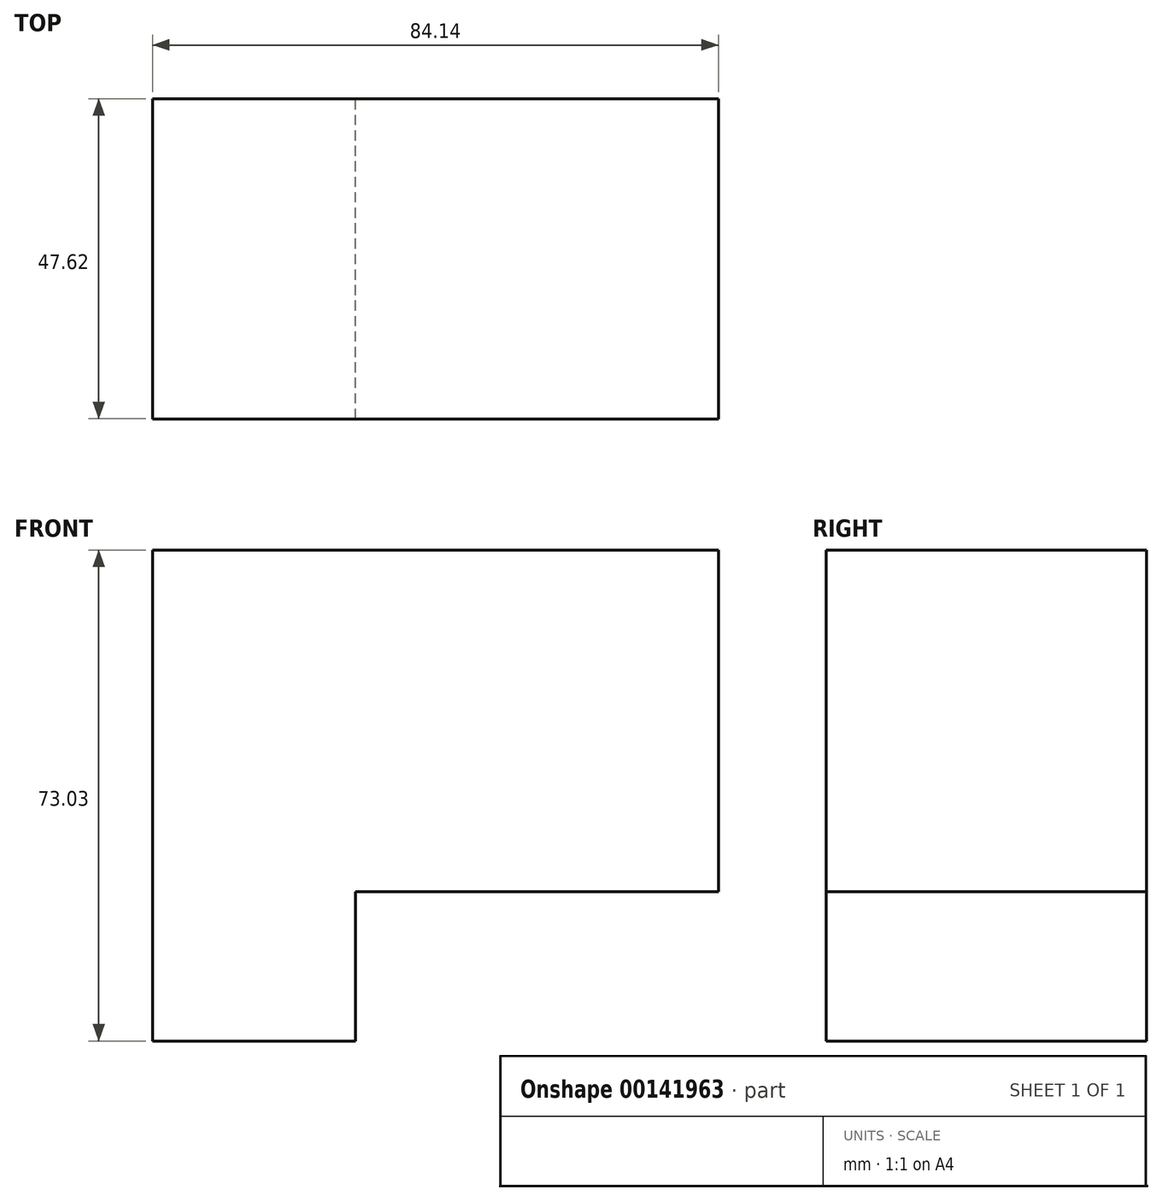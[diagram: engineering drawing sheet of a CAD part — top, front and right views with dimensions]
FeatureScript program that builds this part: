
annotation { "Feature Type Name" : "Feature", "Feature Type Description" : "" }
export const myFeature = defineFeature(function(context is Context, id is Id, definition is map)
    precondition{}
    {
        {
            var Q0;
            Q0=qCreatedBy(makeId("Front.planeOp"),FACE);
            var sketch = newSketch(context, id + "F0", { "sketchPlane" : qUnion([Q0])});
            skLineSegment(sketch, "E0.bottom", {"start": v(-30.16, 50.8) * mm, "end": v(0, 50.8) * mm});
            skLineSegment(sketch, "E0.top", {"start": v(-30.16, -22.23) * mm, "end": v(0, -22.23) * mm});
            skLineSegment(sketch, "E0.left", {"start": v(-30.16, 50.8) * mm, "end": v(-30.16, -22.23) * mm});
            skLineSegment(sketch, "E0.right", {"start": v(0, 50.8) * mm, "end": v(0, -22.23) * mm});
            skLineSegment(sketch, "E1.bottom", {"start": v(0, 50.8) * mm, "end": v(53.97, 50.8) * mm});
            skLineSegment(sketch, "E1.top", {"start": v(0, 0) * mm, "end": v(53.97, 0) * mm});
            skLineSegment(sketch, "E1.left", {"start": v(0, 50.8) * mm, "end": v(0, 0) * mm});
            skLineSegment(sketch, "E1.right", {"start": v(53.97, 50.8) * mm, "end": v(53.97, 0) * mm});
            skSolve(sketch);
        }
        {
            var Q0;
            Q0=makeQuery(id+"F0.imprint","IMPRINT",FACE,{"disambiguationData":[TD([[makeQuery(id+"F0.imprint","IMPRINT",EDGE,{"derivedFrom":sQuery(id+"F0.wireOp",EDGE,"E1.bottom")}),-1.0]])]});
            extrude(context, id + "F1", {"entities" : qUnion([Q0]), "depth" : 47.62 * mm});
        }
        {
            var Q0;
            Q0=makeQuery(id+"F0.imprint","IMPRINT",FACE,{"disambiguationData":[TD([[makeQuery(id+"F0.imprint","IMPRINT",EDGE,{"derivedFrom":sQuery(id+"F0.wireOp",EDGE,"E0.bottom")}),-1.0]])]});
            var Q1;
            Q1=makeQuery(id+"F1.opExtrude","CAP_FACE",FACE,{"disambiguationData":[OSD([sQuery(id+"F0.wireOp",EDGE,"E1.bottom"),sQuery(id+"F0.wireOp",EDGE,"E1.top"),sQuery(id+"F0.wireOp",EDGE,"E1.left"),sQuery(id+"F0.wireOp",EDGE,"E1.right")])],"isStart":false});
            extrude(context, id + "F2", {"entities" : qUnion([Q0]), "operationType" : NewBodyOperationType.ADD, "endBound" : BoundingType.UP_TO_SURFACE, "endBoundEntityFace" : qUnion([Q1]), "depth" : 25.4 * mm});
        }
    });
